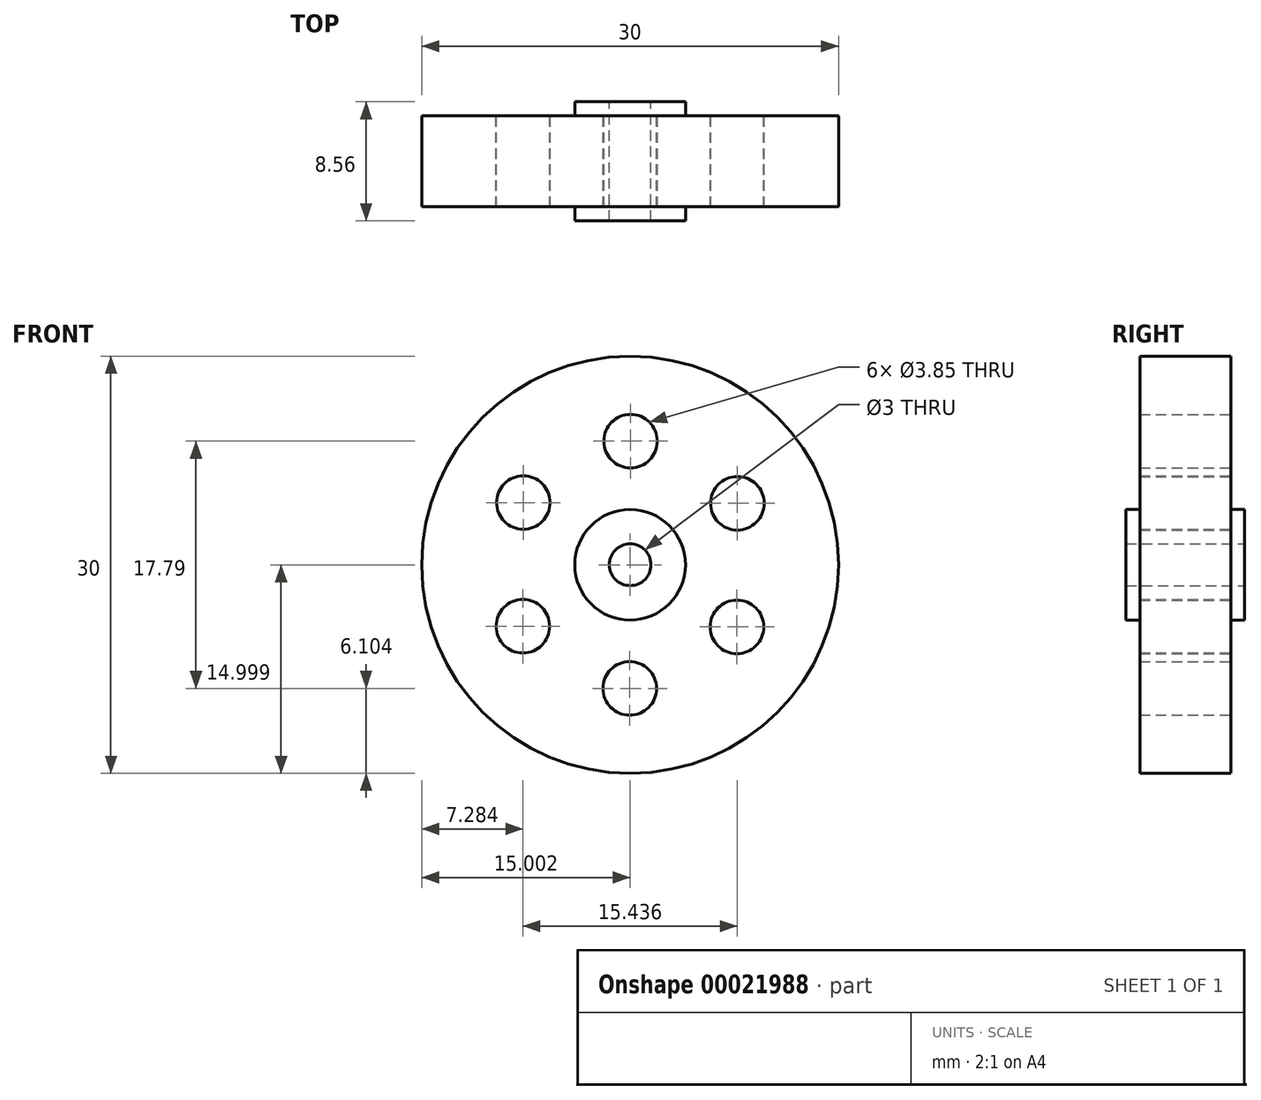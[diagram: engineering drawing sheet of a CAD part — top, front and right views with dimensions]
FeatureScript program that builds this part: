
annotation { "Feature Type Name" : "Feature", "Feature Type Description" : "" }
export const myFeature = defineFeature(function(context is Context, id is Id, definition is map)
    precondition{}
    {
        {
            var Q0;
            Q0=qCreatedBy(makeId("Front.planeOp"),FACE);
            var sketch = newSketch(context, id + "F0", { "sketchPlane" : qUnion([Q0])});
            skCircle(sketch, "E0", {"center": v(-0.3, 0.45) * mm, "radius": 15 * mm});
            skCircle(sketch, "E1", {"center": v(-0.27, 9.34) * mm, "radius": 1.93 * mm});
            skCircle(sketch, "E2.1.0", {"center": v(-7.99, 4.92) * mm, "radius": 1.93 * mm});
            skCircle(sketch, "E2.2.0", {"center": v(-8.02, -3.97) * mm, "radius": 1.93 * mm});
            skCircle(sketch, "E2.3.0", {"center": v(-0.33, -8.45) * mm, "radius": 1.93 * mm});
            skCircle(sketch, "E2.4.0", {"center": v(7.4, -4.02) * mm, "radius": 1.93 * mm});
            skCircle(sketch, "E2.5.0", {"center": v(7.42, 4.87) * mm, "radius": 1.93 * mm});
            skCircle(sketch, "E3", {"center": v(-0.3, 0.45) * mm, "radius": 3.98 * mm});
            skCircle(sketch, "E4", {"center": v(-0.3, 0.45) * mm, "radius": 1.5 * mm});
            skLineSegment(sketch, "E5", {"start": v(-0.3, 4.43) * mm, "end": v(-0.3, 7.42) * mm});
            skSolve(sketch);
        }
        {
            var Q0;
            Q0=makeQuery(id+"F0.imprint","IMPRINT",FACE,{"disambiguationData":[TD([[makeQuery(id+"F0.imprint","IMPRINT",EDGE,{"derivedFrom":sQuery(id+"F0.wireOp",EDGE,"E0")}),1.0]])]});
            extrude(context, id + "F1", {"entities" : qUnion([Q0]), "endBound" : BoundingType.SYMMETRIC, "depth" : 6.55 * mm});
        }
        {
            var Q0;
            Q0=makeQuery(id+"F0.imprint","IMPRINT",FACE,{"disambiguationData":[TD([[makeQuery(id+"F0.imprint","IMPRINT",EDGE,{"derivedFrom":sQuery(id+"F0.wireOp",EDGE,"E3")}),1.0]])]});
            extrude(context, id + "F2", {"entities" : qUnion([Q0]), "operationType" : NewBodyOperationType.ADD, "endBound" : BoundingType.SYMMETRIC, "depth" : 8.55 * mm});
        }
    });
